# Revit family: JOMA_413, 414 & 415
name_source: partatom
category: Structural Connections
revit_build: Autodesk Revit Structure 2012 (Build: 20110309_2315(x64)
units: mm (PartAtom-declared; Revit-internal decimal feet)

## types (3) — shared parameters
Länk Joma Dimensioneringsverktyg = http://www.joma.se
Material = Varmförzinkad stålplåt
ir = 2.562 mm
t = 2 mm  [stored 0.00656168 ft]
yr = 4.562 mm
zero-valued in all types: Default Elevation

## per-type parameters (varying)
| type | Typ | Vikt | Vinkelbeslag 413 | Vinkelbeslag 414 | Vinkelbeslag 415 | b | h | l |
| 4130000 | VINKEL 413 | 0,158 | Yes | No | No | 80 mm  [stored 0.262467 ft] | 65 mm  [stored 0.213255 ft] | 65 mm  [stored 0.213255 ft] |
| 4140000 | VINKEL 414 | 0,158 | No | Yes | No | 80 mm  [stored 0.262467 ft] | 80 mm  [stored 0.262467 ft] | 80 mm  [stored 0.262467 ft] |
| 4150000 | VINKEL 415 | 0,091 | No | No | Yes | 40 mm  [stored 0.131234 ft] | 83 mm  [stored 0.27231 ft] | 62 mm  [stored 0.203412 ft] |

note: [stored X ft] marks values corroborated as IEEE doubles in the binary element streams (Revit-internal decimal feet)

## geometry (parser evidence)
native form markers: Sweep x3
no freeform markers — native parametric forms only
